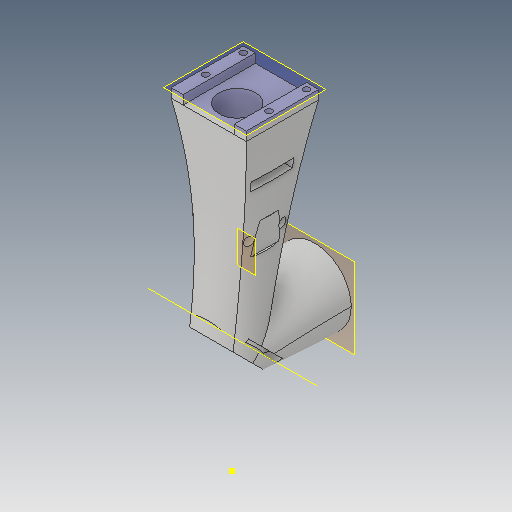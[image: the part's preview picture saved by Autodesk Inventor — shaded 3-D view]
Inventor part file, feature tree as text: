
AUTODESK INVENTOR PART (.ipt)
format: ipt  version: 2019.4 (Build 234330000, 330)  size: 438,784 bytes
history: native  units: mm
features: sketch x14, reference x11, extrude x9, plane x6, other x6, projected_geometry x3, loft x2
ambient origin geometry x8: Origin, YZ Plane, XZ Plane, XY Plane, X Axis, Y Axis, Z Axis, Center Point
bodies: Solid1 (feature_tree)
feature tree (51):
  plane  "Work Plane1"
  extrude  "Extrusion1"  Depth=4.0mm
  sketch  "Sketch2"  dims[d2=1.5mm d3=1.5mm]
  plane  "Work Plane2"
  loft  "Loft1"
  sketch  "Sketch4"  dims[d6=3.0mm d7=0.0mm d8=20.0mm]
  plane  "Work Plane3"
  loft  "Loft2"
  plane  "Work Plane4"
  extrude  "Extrusion2"  Depth=20.0mm
  extrude  "Extrusion3"  Depth=3.0mm TaperAngle=0.0deg
  extrude  "Extrusion4"  Depth=3.0mm TaperAngle=0.0deg
  extrude  "Extrusion5"  Depth=22.0mm
  sketch  "Sketch10"  dims[d31=5.0mm d32=0.0mm d35=0.0mm d36=90.0deg]
  plane  "Work Plane5"
  extrude  "Extrusion6"  Depth=20.0mm
  sketch  "Sketch11"  dims[d37=10.0mm d38=90.0deg d47=10.0mm d48=13.962634mm d49=0.0mm d50=90.0deg]
  plane  "Work Plane6"
  extrude  "Extrusion7"  TaperAngle=60.0deg  [1 undecoded]
  extrude  "Extrusion8"  TaperAngle=0.0deg  [1 undecoded]
  extrude  "Extrusion9"  Depth=10.0mm TaperAngle=0.0deg
  sketch  "Sketch1"  dims[d0=4.0mm d1=4.0mm]
  reference  "Reference1"
  projected_geometry  "Projected Loop1"
  projected_geometry  "Projected Loop2"
  sketch  "Sketch3"  dims[d4=1.5mm d5=1.5mm]
  reference  "Reference2"
  projected_geometry  "Projected Loop3"
  sketch  "Sketch5"  dims[d17=-3.0mm d18=3.0mm d19=0.0mm]
  reference  "Reference3"
  reference  "Reference4"
  sketch  "Sketch6"  dims[d20=16.0mm d21=3.0mm d22=0.0mm]
  reference  "Reference5"
  sketch  "Sketch7"  dims[d23=3.0mm d24=0.0mm d25=22.0mm]
  reference  "Reference6"
  sketch  "Sketch8"  dims[d26=5.0mm d27=0.0mm d28=20.0mm]
  sketch  "Sketch9"  dims[d29=60.0deg d30=60.0deg]
  reference  "Reference7"
  reference  "Reference8"
  sketch  "Sketch12"  dims[d51=5.0mm d52=0.0mm]
  reference  "Reference14"
  reference  "Reference15"
  sketch  "Sketch13"  dims[d53=5.0mm d54=0.0mm]
  reference  "Reference16"
  sketch  "Sketch14"  dims[d55=1.5mm d56=15.0mm d57=3.0mm d58=14.0mm d59=5.0mm d60=0.0mm]
  other  "Assembly_Opentrons_Autofocus_v2.iam"
  other  "00_RasPi_Camera:1"
  other  "00_COMAR_Mirror_10mm:1"
  other  "00_objectivelens_10x:1"
  other  "07_OPENTRONS_Autofocus_objectivemount_v0:1"
  other  "01_Slide_camera_v1:1"
note: 2 required parameter values undecoded (feature->parameter linkage not recoverable at this tier; creation-order binding heuristic only, values carry confidence <= 0.55)
